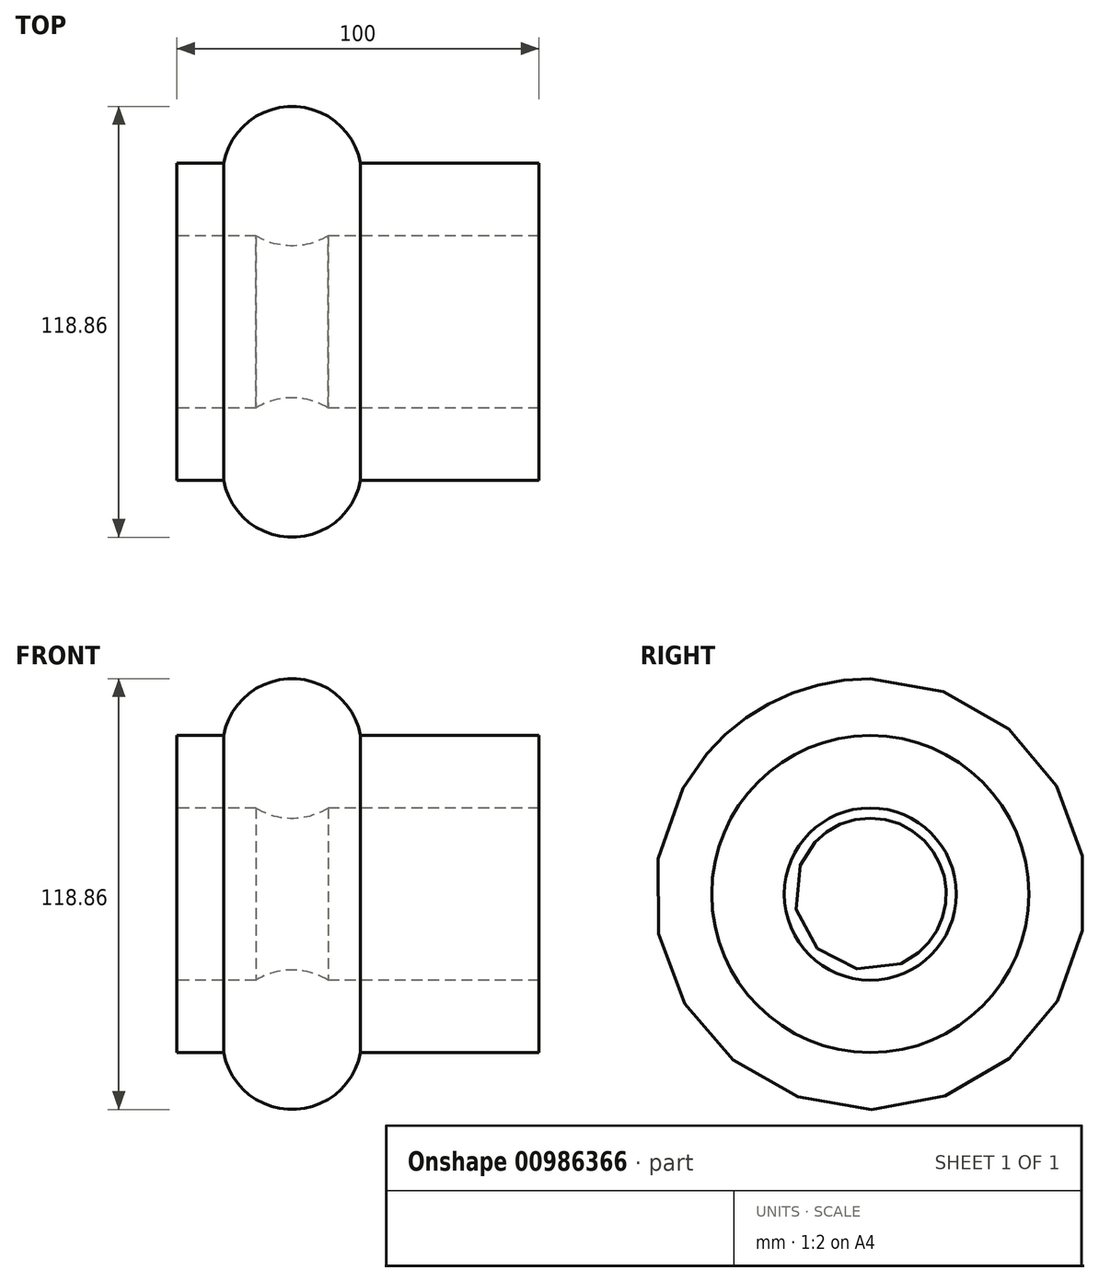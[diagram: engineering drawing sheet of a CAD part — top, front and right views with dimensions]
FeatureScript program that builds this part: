
annotation { "Feature Type Name" : "Feature", "Feature Type Description" : "" }
export const myFeature = defineFeature(function(context is Context, id is Id, definition is map)
    precondition{}
    {
        {
            var Q0;
            Q0=qCreatedBy(makeId("Front.planeOp"),FACE);
            var sketch = newSketch(context, id + "F0", { "sketchPlane" : qUnion([Q0])});
            skLineSegment(sketch, "E0.bottom", {"start": v(-50, 23.75) * mm, "end": v(-28.15, 23.75) * mm});
            skLineSegment(sketch, "E0.top", {"start": v(-50, 43.75) * mm, "end": v(-37.07, 43.75) * mm});
            skLineSegment(sketch, "E0.left", {"start": v(-50, 23.75) * mm, "end": v(-50, 43.75) * mm});
            skLineSegment(sketch, "E0.right", {"start": v(50, 23.75) * mm, "end": v(50, 43.75) * mm});
            skLineSegment(sketch, "E1", {"start": v(-90.15, 0) * mm, "end": v(109.85, 0) * mm});
            skArc(sketch, "E2", {"start": v(-28.15, 23.75) * mm, "mid": v(-18.16, 20.96) * mm, "end": v(-8.18, 23.75) * mm});
            skLineSegment(sketch, "E3.trimOffspring", {"start": v(-8.18, 23.75) * mm, "end": v(50, 23.75) * mm});
            skArc(sketch, "E4.trimOffspring", {"start": v(0.74, 43.75) * mm, "mid": v(-18.16, 59.43) * mm, "end": v(-37.07, 43.75) * mm});
            skLineSegment(sketch, "E5.trimOffspring", {"start": v(0.74, 43.75) * mm, "end": v(50, 43.75) * mm});
            skSolve(sketch);
        }
        {
            var Q0;
            Q0=makeQuery(id+"F0.imprint","IMPRINT",FACE,{"disambiguationData":[TD([[makeQuery(id+"F0.imprint","IMPRINT",EDGE,{"derivedFrom":sQuery(id+"F0.wireOp",EDGE,"E0.bottom")}),1.0]])]});
            var Q1;
            Q1=sQuery(id+"F0.wireOp",EDGE,"E1");
            revolve(context, id + "F1", {"surfaceOperationType" : NewSurfaceOperationType.NEW, "entities" : qUnion([Q0]), "axis" : qUnion([Q1]), "revolveType" : RevolveType.FULL});
        }
    });
